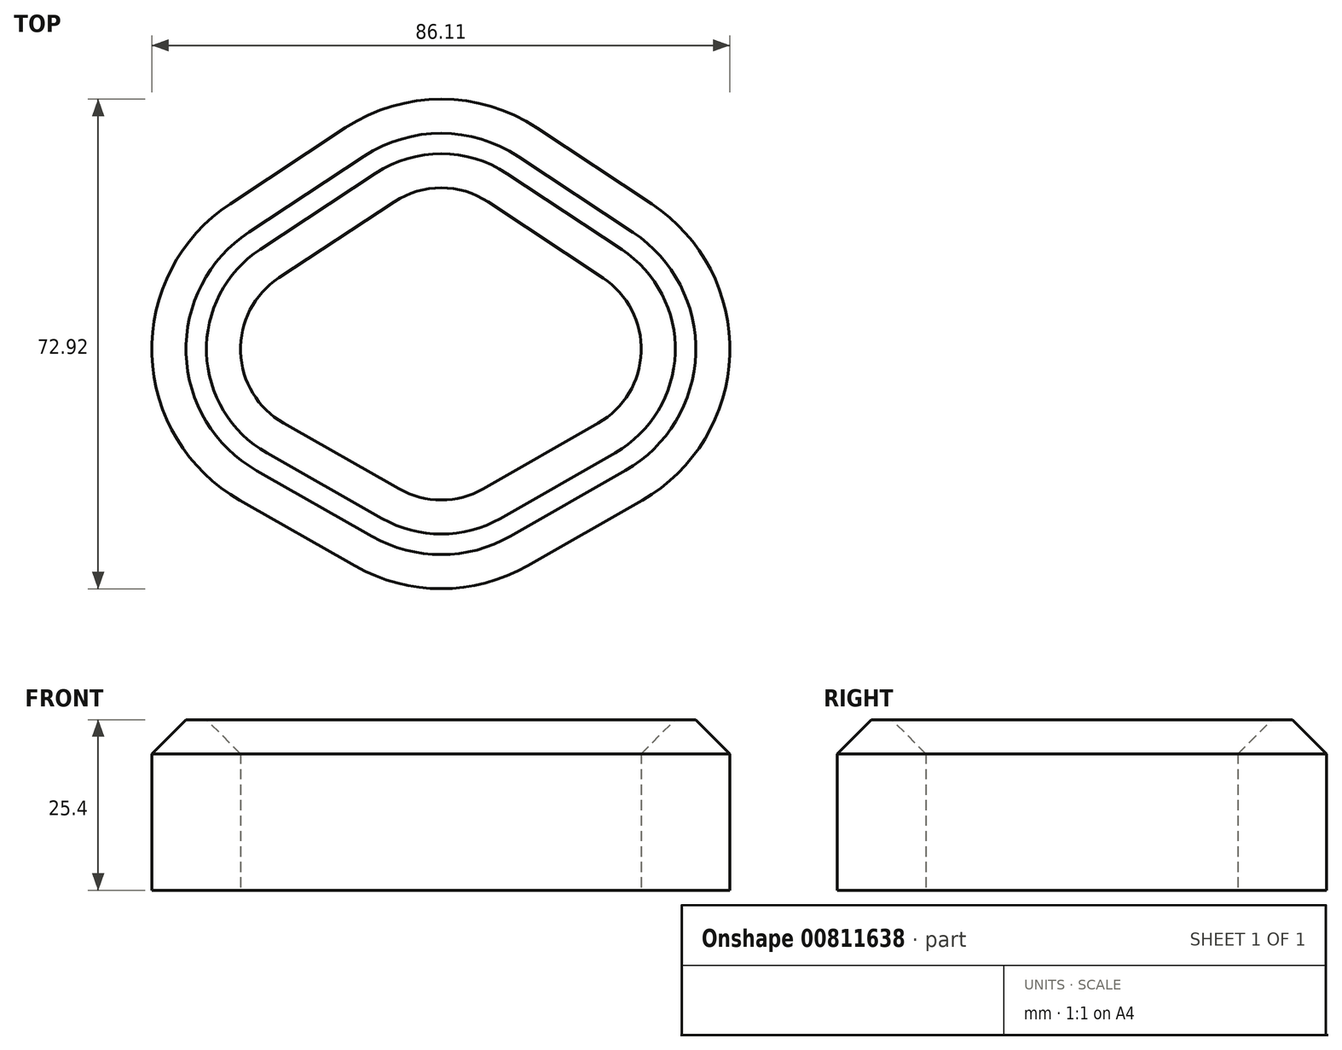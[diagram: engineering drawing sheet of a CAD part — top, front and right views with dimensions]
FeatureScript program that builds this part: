
annotation { "Feature Type Name" : "Feature", "Feature Type Description" : "" }
export const myFeature = defineFeature(function(context is Context, id is Id, definition is map)
    precondition{}
    {
        {
            var Q0;
            Q0=qCreatedBy(makeId("Top.planeOp"),FACE);
            var sketch = newSketch(context, id + "F0", { "sketchPlane" : qUnion([Q0])});
            skLineSegment(sketch, "E0", {"start": v(-24.2, 11.4) * mm, "end": v(-7, 22.72) * mm});
            skLineSegment(sketch, "E1", {"start": v(7, 22.7) * mm, "end": v(24.1, 11.38) * mm});
            skLineSegment(sketch, "E2", {"start": v(23.39, -10.23) * mm, "end": v(6.29, -20.01) * mm});
            skLineSegment(sketch, "E3", {"start": v(-6.3, -20.03) * mm, "end": v(-23.5, -10.25) * mm});
            skPoint(sketch, "E4.visualSharp", {"position": v(0, 27.33) * mm});
            skArc(sketch, "E4.filletArc", {"start": v(7, 22.7) * mm, "mid": v(0, 24.81) * mm, "end": v(-7, 22.72) * mm});
            skPoint(sketch, "E5.visualSharp", {"position": v(-41.52, 0) * mm});
            skArc(sketch, "E5.filletArc", {"start": v(-24.2, 11.4) * mm, "mid": v(-29.9, 0.38) * mm, "end": v(-23.5, -10.25) * mm});
            skPoint(sketch, "E6.visualSharp", {"position": v(0, -23.6) * mm});
            skArc(sketch, "E6.filletArc", {"start": v(-6.3, -20.03) * mm, "mid": v(0, -21.69) * mm, "end": v(6.29, -20.01) * mm});
            skPoint(sketch, "E7.visualSharp", {"position": v(41.28, 0) * mm});
            skArc(sketch, "E7.filletArc", {"start": v(23.39, -10.23) * mm, "mid": v(29.78, 0.38) * mm, "end": v(24.1, 11.38) * mm});
            skArc(sketch, "E8.0", {"start": v(-31.46, 22.43) * mm, "mid": v(-43.11, -0.05) * mm, "end": v(-30.02, -21.73) * mm});
            skLineSegment(sketch, "E8.1", {"start": v(-12.82, -31.5) * mm, "end": v(-30.02, -21.73) * mm});
            skLineSegment(sketch, "E8.2", {"start": v(-31.46, 22.43) * mm, "end": v(-14.26, 33.75) * mm});
            skArc(sketch, "E8.3", {"start": v(-12.82, -31.5) * mm, "mid": v(0.01, -34.9) * mm, "end": v(12.84, -31.48) * mm});
            skArc(sketch, "E8.4", {"start": v(14.28, 33.71) * mm, "mid": v(0.01, 38.02) * mm, "end": v(-14.26, 33.75) * mm});
            skLineSegment(sketch, "E8.5", {"start": v(14.28, 33.71) * mm, "end": v(31.38, 22.4) * mm});
            skArc(sketch, "E8.6", {"start": v(29.94, -21.7) * mm, "mid": v(42.98, -0.06) * mm, "end": v(31.38, 22.4) * mm});
            skLineSegment(sketch, "E8.7", {"start": v(29.94, -21.7) * mm, "end": v(12.84, -31.48) * mm});
            skSolve(sketch);
        }
        {
            var Q0;
            Q0 = qSketchRegion(id + "F0", true);
            extrude(context, id + "F1", {"entities" : qUnion([Q0]), "depth" : 25.4 * mm, "offsetDistance" : 25.4 * mm});
        }
        {
            var Q0;
            Q0=makeQuery(id+"F1.opExtrude","CAP_FACE",FACE,{"disambiguationData":[OSD([sQuery(id+"F0.wireOp",EDGE,"E0"),sQuery(id+"F0.wireOp",EDGE,"E1"),sQuery(id+"F0.wireOp",EDGE,"E2"),sQuery(id+"F0.wireOp",EDGE,"E3"),sQuery(id+"F0.wireOp",EDGE,"E4.filletArc"),sQuery(id+"F0.wireOp",EDGE,"E5.filletArc"),sQuery(id+"F0.wireOp",EDGE,"E6.filletArc"),sQuery(id+"F0.wireOp",EDGE,"E7.filletArc"),sQuery(id+"F0.wireOp",EDGE,"E8.0"),sQuery(id+"F0.wireOp",EDGE,"E8.1"),sQuery(id+"F0.wireOp",EDGE,"E8.2"),sQuery(id+"F0.wireOp",EDGE,"E8.3"),sQuery(id+"F0.wireOp",EDGE,"E8.4"),sQuery(id+"F0.wireOp",EDGE,"E8.5"),sQuery(id+"F0.wireOp",EDGE,"E8.6"),sQuery(id+"F0.wireOp",EDGE,"E8.7")])],"isStart":false});
            chamfer(context, id + "F2", {"entities" : qUnion([Q0]), "width" : 5.08 * mm, "tangentPropagation" : true});
        }
    });
